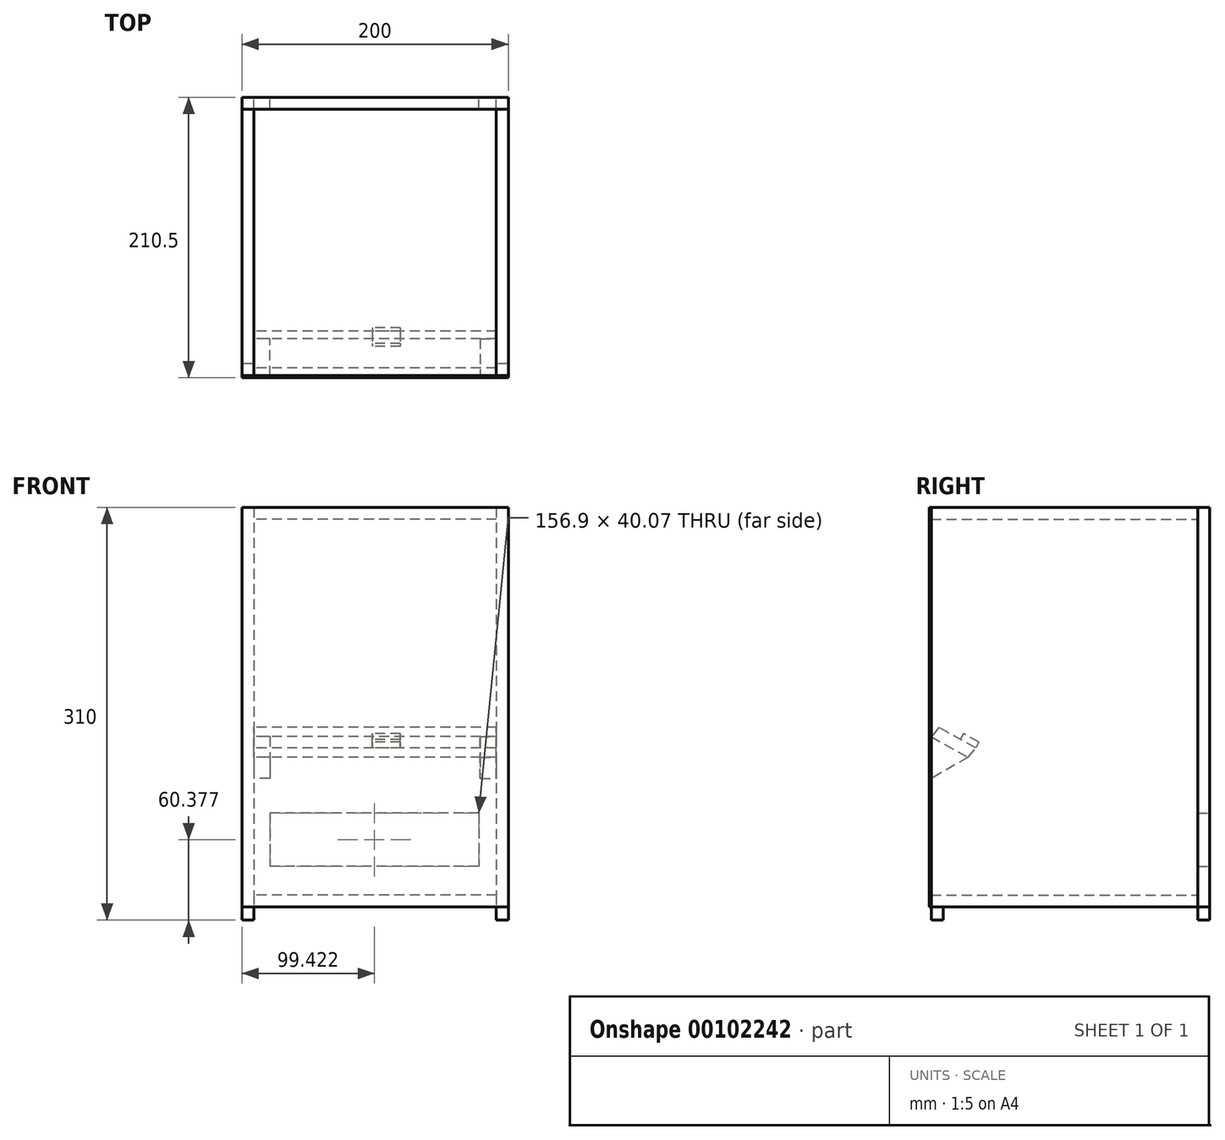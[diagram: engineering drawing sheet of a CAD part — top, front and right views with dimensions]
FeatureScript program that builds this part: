
annotation { "Feature Type Name" : "Feature", "Feature Type Description" : "" }
export const myFeature = defineFeature(function(context is Context, id is Id, definition is map)
    precondition{}
    {
        {
            var Q0;
            Q0=qCreatedBy(makeId("Front.planeOp"),FACE);
            var sketch = newSketch(context, id + "F0", { "sketchPlane" : qUnion([Q0])});
            skLineSegment(sketch, "E0.bottom", {"start": v(0, 0) * mm, "end": v(200, 0) * mm});
            skLineSegment(sketch, "E0.top", {"start": v(0, 300) * mm, "end": v(200, 300) * mm});
            skLineSegment(sketch, "E0.left", {"start": v(0, 0) * mm, "end": v(0, 300) * mm});
            skLineSegment(sketch, "E0.right", {"start": v(200, 0) * mm, "end": v(200, 300) * mm});
            skSolve(sketch);
        }
        {
            var Q0;
            Q0=qSketchRegion(id+"F0",true);
            extrude(context, id + "F1", {"entities" : qUnion([Q0]), "depth" : 1.5 * mm});
        }
        {
            var Q0;
            Q0=makeQuery(id+"F1.opExtrude","CAP_FACE",FACE,{"disambiguationData":[OSD([sQuery(id+"F0.wireOp",EDGE,"E0.bottom"),sQuery(id+"F0.wireOp",EDGE,"E0.top"),sQuery(id+"F0.wireOp",EDGE,"E0.left"),sQuery(id+"F0.wireOp",EDGE,"E0.right")])],"isStart":true});
            var sketch = newSketch(context, id + "F2", { "sketchPlane" : qUnion([Q0])});
            skLineSegment(sketch, "E1.bottom", {"start": v(0, 300) * mm, "end": v(-9, 300) * mm});
            skLineSegment(sketch, "E1.top", {"start": v(0, 0) * mm, "end": v(-9, 0) * mm});
            skLineSegment(sketch, "E1.left", {"start": v(0, 300) * mm, "end": v(0, 0) * mm});
            skLineSegment(sketch, "E1.right", {"start": v(-9, 300) * mm, "end": v(-9, 0) * mm});
            skSolve(sketch);
        }
        {
            var Q0;
            Q0=qSketchRegion(id+"F2",true);
            extrude(context, id + "F3", {"entities" : qUnion([Q0]), "depth" : 200 * mm});
        }
        {
            var Q0;
            Q0=makeQuery(id+"F3.opExtrude","SWEPT_FACE",FACE,{"disambiguationData":[OSD([sQuery(id+"F2.wireOp",EDGE,"E1.right")])]});
            var sketch = newSketch(context, id + "F4", { "sketchPlane" : qUnion([Q0])});
            skLineSegment(sketch, "E2", {"start": v(0, 96.36) * mm, "end": v(0, 127.78) * mm});
            skLineSegment(sketch, "E3", {"start": v(0, 127.78) * mm, "end": v(27.68, 112.25) * mm});
            skLineSegment(sketch, "E4", {"start": v(27.68, 112.25) * mm, "end": v(0, 96.36) * mm});
            skSolve(sketch);
        }
        {
            var Q0;
            Q0=qSketchRegion(id+"F4",true);
            extrude(context, id + "F5", {"entities" : qUnion([Q0]), "depth" : 12 * mm});
        }
        {
            var Q0;
            Q0=makeQuery(id+"F3.opExtrude","SWEPT_FACE",FACE,{"disambiguationData":[OSD([sQuery(id+"F2.wireOp",EDGE,"E1.right")])]});
            var sketch = newSketch(context, id + "F6", { "sketchPlane" : qUnion([Q0])});
            skLineSegment(sketch, "E5", {"start": v(27.68, 112.25) * mm, "end": v(33.36, 119.32) * mm});
            skLineSegment(sketch, "E6", {"start": v(33.36, 119.32) * mm, "end": v(5.69, 134.85) * mm});
            skLineSegment(sketch, "E7", {"start": v(5.69, 134.85) * mm, "end": v(0, 127.78) * mm});
            skLineSegment(sketch, "E8", {"start": v(0, 127.78) * mm, "end": v(27.68, 112.25) * mm});
            skSolve(sketch);
        }
        {
            var Q0;
            Q0=qSketchRegion(id+"F6",true);
            extrude(context, id + "F7", {"entities" : qUnion([Q0]), "depth" : 182 * mm});
        }
        {
            var Q0;
            Q0=makeQuery(id+"F7.opExtrude","SWEPT_FACE",FACE,{"disambiguationData":[OSD([sQuery(id+"F6.wireOp",EDGE,"E6")])]});
            var sketch = newSketch(context, id + "F8", { "sketchPlane" : qUnion([Q0])});
            skLineSegment(sketch, "E9.bottom", {"start": v(118.97, -29.3) * mm, "end": v(97.76, -29.3) * mm});
            skLineSegment(sketch, "E9.top", {"start": v(118.97, -42.52) * mm, "end": v(97.76, -42.52) * mm});
            skLineSegment(sketch, "E9.left", {"start": v(118.97, -29.3) * mm, "end": v(118.97, -42.52) * mm});
            skLineSegment(sketch, "E9.right", {"start": v(97.76, -29.3) * mm, "end": v(97.76, -42.52) * mm});
            skSolve(sketch);
        }
        {
            var Q0;
            Q0 = qSketchRegion(id + "F8", true);
            extrude(context, id + "F9", {"entities" : qUnion([Q0]), "depth" : 5 * mm});
        }
        {
            var Q0;
            Q0=makeQuery(id+"F7.opExtrude","CAP_FACE",FACE,{"disambiguationData":[OSD([sQuery(id+"F6.wireOp",EDGE,"E5"),sQuery(id+"F6.wireOp",EDGE,"E6"),sQuery(id+"F6.wireOp",EDGE,"E7"),sQuery(id+"F6.wireOp",EDGE,"E8")])],"isStart":false});
            var sketch = newSketch(context, id + "F10", { "sketchPlane" : qUnion([Q0])});
            skLineSegment(sketch, "E10", {"start": v(0, 96.36) * mm, "end": v(0, 127.78) * mm});
            skLineSegment(sketch, "E11", {"start": v(0, 127.78) * mm, "end": v(27.68, 112.25) * mm});
            skLineSegment(sketch, "E12", {"start": v(27.68, 112.25) * mm, "end": v(0, 96.36) * mm});
            skSolve(sketch);
        }
        {
            var Q0;
            Q0 = qSketchRegion(id + "F10", true);
            extrude(context, id + "F11", {"entities" : qUnion([Q0]), "oppositeDirection" : true, "depth" : 12 * mm});
        }
        {
            var Q0;
            Q0=makeQuery(id+"F3.opExtrude","SWEPT_FACE",FACE,{"disambiguationData":[OSD([sQuery(id+"F2.wireOp",EDGE,"E1.right")])]});
            var sketch = newSketch(context, id + "F12", { "sketchPlane" : qUnion([Q0])});
            skLineSegment(sketch, "E13.bottom", {"start": v(0, 300) * mm, "end": v(200, 300) * mm});
            skLineSegment(sketch, "E13.top", {"start": v(0, 291) * mm, "end": v(200, 291) * mm});
            skLineSegment(sketch, "E13.left", {"start": v(0, 300) * mm, "end": v(0, 291) * mm});
            skLineSegment(sketch, "E13.right", {"start": v(200, 300) * mm, "end": v(200, 291) * mm});
            skSolve(sketch);
        }
        {
            var Q0;
            Q0 = qSketchRegion(id + "F12", true);
            extrude(context, id + "F13", {"entities" : qUnion([Q0]), "depth" : 182 * mm});
        }
        {
            var Q0;
            Q0=makeQuery(id+"F3.opExtrude","SWEPT_FACE",FACE,{"disambiguationData":[OSD([sQuery(id+"F2.wireOp",EDGE,"E1.right")])]});
            var sketch = newSketch(context, id + "F14", { "sketchPlane" : qUnion([Q0])});
            skLineSegment(sketch, "E14.bottom", {"start": v(0, 0) * mm, "end": v(200, 0) * mm});
            skLineSegment(sketch, "E14.top", {"start": v(0, 9) * mm, "end": v(200, 9) * mm});
            skLineSegment(sketch, "E14.left", {"start": v(0, 0) * mm, "end": v(0, 9) * mm});
            skLineSegment(sketch, "E14.right", {"start": v(200, 0) * mm, "end": v(200, 9) * mm});
            skSolve(sketch);
        }
        {
            var Q0;
            Q0 = qSketchRegion(id + "F14", true);
            extrude(context, id + "F15", {"entities" : qUnion([Q0]), "depth" : 182 * mm});
        }
        {
            var Q0;
            Q0=makeQuery(id+"F13.opExtrude","CAP_FACE",FACE,{"disambiguationData":[OSD([sQuery(id+"F12.wireOp",EDGE,"E13.bottom"),sQuery(id+"F12.wireOp",EDGE,"E13.top"),sQuery(id+"F12.wireOp",EDGE,"E13.left"),sQuery(id+"F12.wireOp",EDGE,"E13.right")])],"isStart":false});
            var sketch = newSketch(context, id + "F16", { "sketchPlane" : qUnion([Q0])});
            skLineSegment(sketch, "E15.bottom", {"start": v(200, 300) * mm, "end": v(0, 300) * mm});
            skLineSegment(sketch, "E15.top", {"start": v(200, 0) * mm, "end": v(0, 0) * mm});
            skLineSegment(sketch, "E15.left", {"start": v(200, 300) * mm, "end": v(200, 0) * mm});
            skLineSegment(sketch, "E15.right", {"start": v(0, 300) * mm, "end": v(0, 0) * mm});
            skSolve(sketch);
        }
        {
            var Q0;
            Q0 = qSketchRegion(id + "F16", true);
            extrude(context, id + "F17", {"entities" : qUnion([Q0]), "depth" : 9 * mm});
        }
        {
            var Q0;
            Q0=makeQuery(id+"F17.opExtrude","SWEPT_FACE",FACE,{"disambiguationData":[OSD([sQuery(id+"F16.wireOp",EDGE,"E15.left")])]});
            var sketch = newSketch(context, id + "F18", { "sketchPlane" : qUnion([Q0])});
            skLineSegment(sketch, "E16.bottom", {"start": v(-200, 300) * mm, "end": v(0, 300) * mm});
            skLineSegment(sketch, "E16.top", {"start": v(-200, 0) * mm, "end": v(0, 0) * mm});
            skLineSegment(sketch, "E16.left", {"start": v(-200, 300) * mm, "end": v(-200, 0) * mm});
            skLineSegment(sketch, "E16.right", {"start": v(0, 300) * mm, "end": v(0, 0) * mm});
            skSolve(sketch);
        }
        {
            var Q0;
            Q0 = qSketchRegion(id + "F18", true);
            extrude(context, id + "F19", {"entities" : qUnion([Q0]), "depth" : 9 * mm});
        }
        {
            var Q0;
            Q0=makeQuery(id+"F19.opExtrude","CAP_FACE",FACE,{"disambiguationData":[OSD([sQuery(id+"F18.wireOp",EDGE,"E16.bottom"),sQuery(id+"F18.wireOp",EDGE,"E16.top"),sQuery(id+"F18.wireOp",EDGE,"E16.left"),sQuery(id+"F18.wireOp",EDGE,"E16.right")])],"isStart":false});
            var sketch = newSketch(context, id + "F20", { "sketchPlane" : qUnion([Q0])});
            skLineSegment(sketch, "E17.bottom", {"start": v(-177.87, 70.41) * mm, "end": v(-20.97, 70.41) * mm});
            skLineSegment(sketch, "E17.top", {"start": v(-177.87, 30.34) * mm, "end": v(-20.97, 30.34) * mm});
            skLineSegment(sketch, "E17.left", {"start": v(-177.87, 70.41) * mm, "end": v(-177.87, 30.34) * mm});
            skLineSegment(sketch, "E17.right", {"start": v(-20.97, 70.41) * mm, "end": v(-20.97, 30.34) * mm});
            skSolve(sketch);
        }
        {
            var Q0;
            Q0 = qSketchRegion(id + "F20", true);
            extrude(context, id + "F21", {"entities" : qUnion([Q0]), "operationType" : NewBodyOperationType.REMOVE, "oppositeDirection" : true, "depth" : 9 * mm});
        }
        {
            var Q0;
            Q0=makeQuery(id+"F17.opExtrude","SWEPT_FACE",FACE,{"disambiguationData":[OSD([sQuery(id+"F16.wireOp",EDGE,"E15.top")])]});
            var sketch = newSketch(context, id + "F22", { "sketchPlane" : qUnion([Q0])});
            skLineSegment(sketch, "E18.bottom", {"start": v(200, 0) * mm, "end": v(191, 0) * mm});
            skLineSegment(sketch, "E18.top", {"start": v(200, -9) * mm, "end": v(191, -9) * mm});
            skLineSegment(sketch, "E18.left", {"start": v(200, 0) * mm, "end": v(200, -9) * mm});
            skLineSegment(sketch, "E18.right", {"start": v(191, 0) * mm, "end": v(191, -9) * mm});
            skLineSegment(sketch, "E19.bottom", {"start": v(200, -200) * mm, "end": v(191, -200) * mm});
            skLineSegment(sketch, "E19.top", {"start": v(200, -209) * mm, "end": v(191, -209) * mm});
            skLineSegment(sketch, "E19.left", {"start": v(200, -200) * mm, "end": v(200, -209) * mm});
            skLineSegment(sketch, "E19.right", {"start": v(191, -200) * mm, "end": v(191, -209) * mm});
            skLineSegment(sketch, "E20.bottom", {"start": v(9, -200) * mm, "end": v(0, -200) * mm});
            skLineSegment(sketch, "E20.top", {"start": v(9, -209) * mm, "end": v(0, -209) * mm});
            skLineSegment(sketch, "E20.left", {"start": v(9, -200) * mm, "end": v(9, -209) * mm});
            skLineSegment(sketch, "E20.right", {"start": v(0, -200) * mm, "end": v(0, -209) * mm});
            skLineSegment(sketch, "E21.bottom", {"start": v(9, 0) * mm, "end": v(0, 0) * mm});
            skLineSegment(sketch, "E21.top", {"start": v(9, -9) * mm, "end": v(0, -9) * mm});
            skLineSegment(sketch, "E21.left", {"start": v(9, 0) * mm, "end": v(9, -9) * mm});
            skLineSegment(sketch, "E21.right", {"start": v(0, 0) * mm, "end": v(0, -9) * mm});
            skSolve(sketch);
        }
        {
            var Q0;
            Q0 = qSketchRegion(id + "F22", true);
            extrude(context, id + "F23", {"entities" : qUnion([Q0]), "depth" : 10 * mm});
        }
    });
